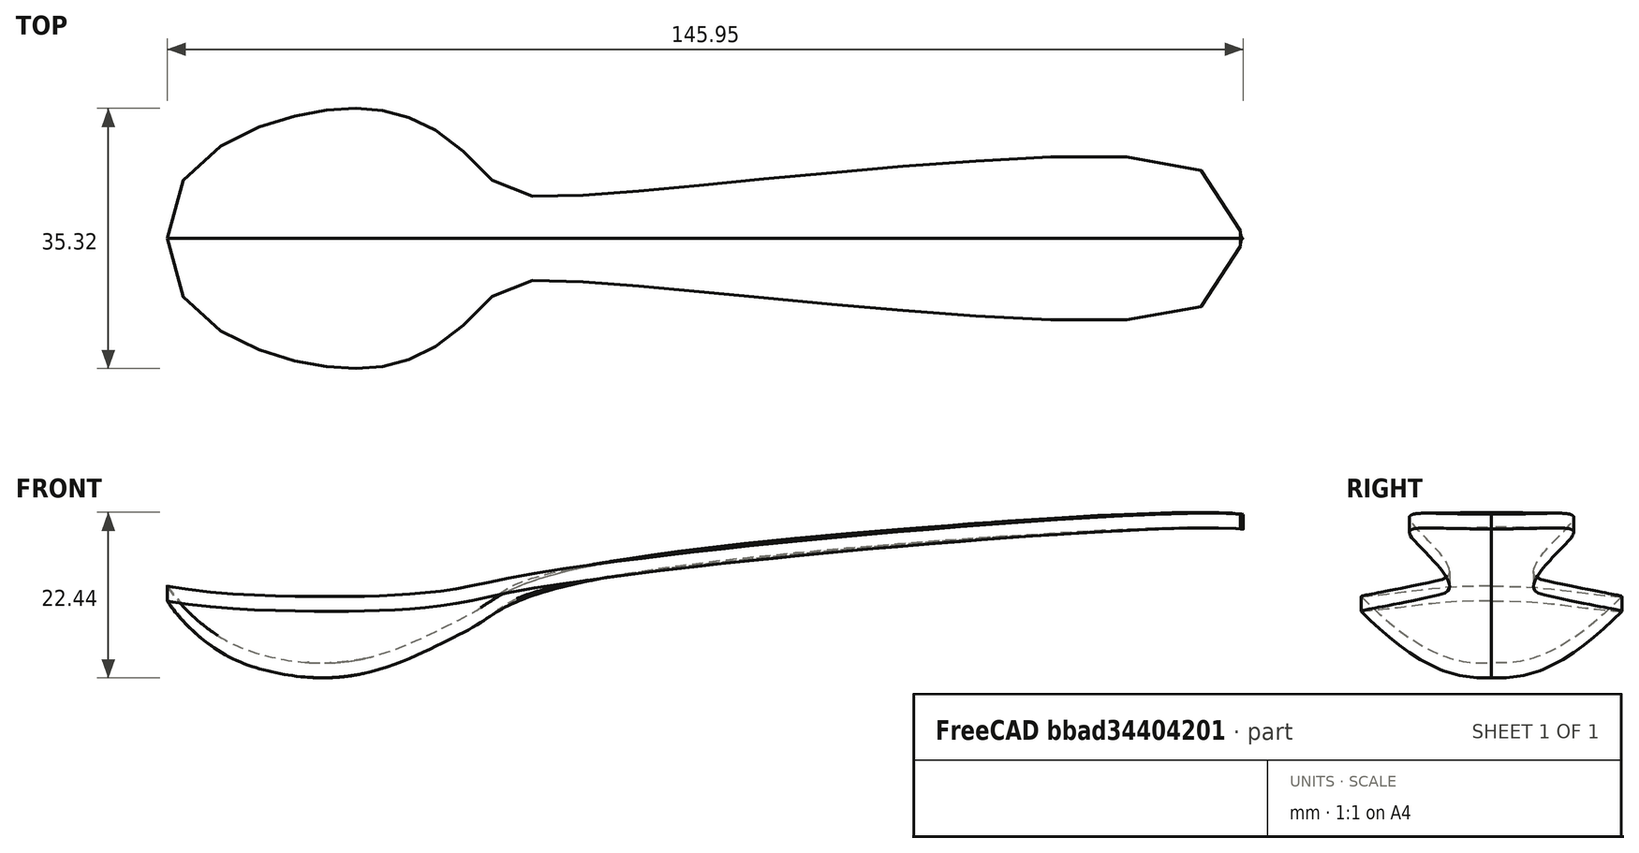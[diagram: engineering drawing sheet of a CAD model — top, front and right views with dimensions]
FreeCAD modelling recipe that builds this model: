
FCSTD DOCUMENT  (FreeCAD 0.20R29603 (Git))
Label: spoonFinalUsingCurves
License: All rights reserved
LicenseURL: http://en.wikipedia.org/wiki/All_rights_reserved
objects: Part::FeaturePython×9, Sketcher::SketchObject×7, App::LinkGroup×2, PartDesign::Body×1, Part::Extrusion×1, Part::Mirroring×1, Part::MultiFuse×1
note: 20 computed .brp shape members not serialized (recipe doc carries the construction recipe); baked Part::Feature solids carry a one-line shape summary decoded from their .brp

FEATURE [Sketcher::SketchObject] Sketch  label="top"
  FullyConstrained = false
  MapMode = 5
  Support = -> [XY_Plane]
  sketch-geometry (29):
    g0-g10: Circle x11 (B-spline internal-alignment scaffolding for g11; pole/knot coordinates omitted)
    g11: BSplineCurve PolesCount=11 KnotsCount=9 Degree=3 IsPeriodic=0
    g12: GeomPoint X=-47.6871 Y=0 Z=0
    g13-g20: GeomPoint x8 (B-spline internal-alignment scaffolding for g11; pole/knot coordinates omitted)
    g21: LineSegment StartX=-47.6871 StartY=0 StartZ=0 EndX=97.8729 EndY=0 EndZ=0
    g22: GeomPoint X=-43.3739 Y=0 Z=0
    g23: GeomPoint X=-33.1869 Y=0 Z=0
    g24: GeomPoint X=-21.4164 Y=0 Z=0
    g25: GeomPoint X=-10.9538 Y=0 Z=0
    g26: GeomPoint X=-2.80499 Y=0 Z=0
    g27: GeomPoint X=89.548 Y=0 Z=0
    g28: GeomPoint X=1.42031 Y=0 Z=0
  constraints (18):
    c: Equal(g0, g1-g10) x10
    c: InternalAlignment(g0-g10 -> g11) x11
    c: InternalAlignment(g13-g20 -> g11) x8
    c: Vertical(g11,g1)
    c: Coincident(g11,g12)
    c: Vertical(g9,g11)
    c: DistanceX(g11,g11) = 145.56
    c: PointOnObject(g11,g-1)
    c: Coincident(g21,g11)
    c: Coincident(g21,g11)
    c: Horizontal(g21)
    c: PointOnObject(g22,g21)
    c: PointOnObject(g23,g21)
    c: PointOnObject(g24,g21)
    c: PointOnObject(g25,g21)
    c: PointOnObject(g26,g21)
    c: PointOnObject(g27,g21)
    c: PointOnObject(g28,g21)
FEATURE [PartDesign::Body] Body
  Group = -> [Sketch]
  Origin = -> Origin
FEATURE [Sketcher::SketchObject] Sketch004  label="frontMiddle"
  ExternalGeometry = -> [Sketch]
  FullyConstrained = false
  Placement = pos=(0,0,-1) rot=(1,0,0;1.5708rad)
  sketch-geometry (21):
    g0: GeomPoint X=229.589 Y=93.1021 Z=0
    g1: GeomPoint X=229.589 Y=93.1021 Z=0
    g2: GeomPoint X=229.589 Y=93.1021 Z=0
    g3: GeomPoint X=301.189 Y=90.2757 Z=0
    g4-g12: Circle x9 (B-spline internal-alignment scaffolding for g13; pole/knot coordinates omitted)
    g13: BSplineCurve PolesCount=9 KnotsCount=7 Degree=3 IsPeriodic=0
    g14-g20: GeomPoint x7 (B-spline internal-alignment scaffolding for g13; pole/knot coordinates omitted)
  constraints (5):
    c: Weight(g4) = 1
    c: Coincident(g13,g-3)
    c: Equal(g4, g5-g12) x8
    c: InternalAlignment(g4-g12 -> g13) x9
    c: InternalAlignment(g14-g20 -> g13) x7
FEATURE [Sketcher::SketchObject] Sketch005  label="ffrontSide"
  AttachmentOffset = pos=(0,0,-20) rot=(0,0,1;0rad)
  ExternalGeometry = -> [Sketch,Sketch004]
  FullyConstrained = false
  MapMode = 3
  Placement = pos=(0,20,-4.4e-15) rot=(1,0,0;1.5708rad)
  Support = -> [Sketch]
  sketch-geometry (18):
    g0-g8: Circle x9 (B-spline internal-alignment scaffolding for g9; pole/knot coordinates omitted)
    g9: BSplineCurve PolesCount=9 KnotsCount=7 Degree=3 IsPeriodic=0
    g10-g16: GeomPoint x7 (B-spline internal-alignment scaffolding for g9; pole/knot coordinates omitted)
    g17: LineSegment StartX=98.2633 StartY=9.6068 StartZ=0 EndX=98.2633 EndY=0 EndZ=0
  constraints (7):
    c: Weight(g0) = 1
    c: Equal(g0, g1-g8) x8
    c: InternalAlignment(g0-g8 -> g9) x9
    c: InternalAlignment(g10-g16 -> g9) x7
    c: Coincident(g17,g9)
    c: Vertical(g17)
    c: Coincident(g-4,g9)
FEATURE [Part::FeaturePython] Mixed_curve  label="MixedMiddle"  # WARN: FeaturePython — macro-defined, semantics opaque (R4)
  Active = false
  ApproxTolerance = 0.001
  Continuity = 5
  DegreeMax = 5
  DegreeMin = 3
  Direction1 = (0,0,0)
  Direction2 = (0,0,0)
  FillFace1 = false
  FillFace2 = false
  Parametrization = 0
  Samples = 100
  Shape1 = -> Sketch004
  Shape2 = -> Sketch
FEATURE [Part::FeaturePython] Mixed_curve001  label="MixedSide"  # WARN: FeaturePython — macro-defined, semantics opaque (R4)
  Active = false
  ApproxTolerance = 0.001
  Continuity = 5
  DegreeMax = 5
  DegreeMin = 3
  Direction1 = (0,0,0)
  Direction2 = (0,0,0)
  FillFace1 = false
  FillFace2 = false
  Parametrization = 0
  Samples = 100
  Shape1 = -> Sketch005
  Shape2 = -> Sketch
FEATURE [Part::FeaturePython] Line  # WARN: FeaturePython — macro-defined, semantics opaque (R4)
  Vertex1 = -> Mixed_curve001 [Vertex1]
  Vertex2 = -> Sketch004 [Vertex1]
FEATURE [Part::FeaturePython] Line001  # WARN: FeaturePython — macro-defined, semantics opaque (R4)
  Vertex1 = -> Mixed_curve001 [Vertex2]
  Vertex2 = -> Sketch004 [Vertex2]
FEATURE [Part::FeaturePython] Profile  label="Profile1"  # WARN: FeaturePython — macro-defined, semantics opaque (R4)
  Edge1 = -> Mixed_curve001 [Edge1]
  Edge2 = -> Sketch004 [Edge1]
  MainAxis = (0,0,0)
  Parameter1 = 0.07
  Parameter2 = 0.069036
FEATURE [Part::FeaturePython] Profile001  label="Profile2 "  # WARN: FeaturePython — macro-defined, semantics opaque (R4)
  Edge1 = -> Mixed_curve001 [Edge1]
  Edge2 = -> Sketch004 [Edge1]
  MainAxis = (0,0,0)
  Parameter1 = 0.17
  Parameter2 = 0.269316
FEATURE [Part::FeaturePython] Profile002  label="Profile3"  # WARN: FeaturePython — macro-defined, semantics opaque (R4)
  Edge1 = -> Mixed_curve001 [Edge1]
  Edge2 = -> Sketch004 [Edge1]
  MainAxis = (0,0,0)
  Parameter1 = 0.291991
  Parameter2 = 0.599792
FEATURE [Part::FeaturePython] Profile003  label="Profile4"  # WARN: FeaturePython — macro-defined, semantics opaque (R4)
  Edge1 = -> Mixed_curve001 [Edge1]
  Edge2 = -> Sketch004 [Edge1]
  MainAxis = (0,0,-1)
  Parameter1 = 0.8965
  Parameter2 = 0.965683
FEATURE [Sketcher::SketchObject] Sketch012  label="Sketch1"
  ExternalGeometry = -> [Profile]
  FullyConstrained = false
  MapMode = 5
  Placement = pos=(-41.9192,-2.03518,0) rot=(0.55868,0.586462,0.586462;2.12263rad)
  Support = -> [Profile]
  sketch-geometry (11):
    g0: GeomPoint X=-117.774 Y=-70.6272 Z=0
    g1: GeomPoint X=-117.774 Y=-70.6272 Z=0
    g2: GeomPoint X=-117.774 Y=-70.6272 Z=0
    g3: GeomPoint X=-69.665 Y=-60.183 Z=0
    g4-g7: Circle x4 (B-spline internal-alignment scaffolding for g8; pole/knot coordinates omitted)
    g8: BSplineCurve PolesCount=4 KnotsCount=2 Degree=3 IsPeriodic=0
    g9: GeomPoint X=13.0771 Y=-0.861292 Z=0
    g10: GeomPoint X=2.03758 Y=-6.01694 Z=0
  constraints (10):
    c: Weight(g4) = 1
    c: Coincident(g8,g-3)
    c: Equal(g4,g5)
    c: Equal(g4,g6)
    c: Equal(g4,g7)
    c: Coincident(g8,g-3)
    c: InternalAlignment(g4-g7 -> g8) x4
    c: InternalAlignment(g9,g8)
    c: InternalAlignment(g10,g8)
    c: Horizontal(g6,g8)
FEATURE [Sketcher::SketchObject] Sketch013  label="Sketch2"
  ExternalGeometry = -> [Profile001]
  FullyConstrained = false
  MapMode = 5
  Placement = pos=(-26.1161,0.530872,0) rot=(0.585173,0.573399,0.573399;2.0827rad)
  Support = -> [Profile001]
  sketch-geometry (7):
    g0-g3: Circle x4 (B-spline internal-alignment scaffolding for g4; pole/knot coordinates omitted)
    g4: BSplineCurve PolesCount=4 KnotsCount=2 Degree=3 IsPeriodic=0
    g5: GeomPoint X=16.9177 Y=-1.53827 Z=0
    g6: GeomPoint X=-0.530981 Y=-10.5595 Z=0
  constraints (10):
    c: Weight(g0) = 1
    c: Coincident(g4,g-3)
    c: Equal(g0,g1)
    c: Equal(g0,g2)
    c: Equal(g0,g3)
    c: Coincident(g4,g-3)
    c: InternalAlignment(g0-g3 -> g4) x4
    c: InternalAlignment(g5,g4)
    c: InternalAlignment(g6,g4)
    c: Horizontal(g2,g4)
FEATURE [Sketcher::SketchObject] Sketch014  label="Sketch3"
  ExternalGeometry = -> [Profile002]
  FullyConstrained = false
  MapMode = 5
  Placement = pos=(-5.92794,-0.275172,0) rot=(0.559498,0.586072,0.586072;2.12138rad)
  Support = -> [Profile002]
  sketch-geometry (7):
    g0-g3: Circle x4 (B-spline internal-alignment scaffolding for g4; pole/knot coordinates omitted)
    g4: BSplineCurve PolesCount=4 KnotsCount=2 Degree=3 IsPeriodic=0
    g5: GeomPoint X=10.9999 Y=-0.103713 Z=0
    g6: GeomPoint X=0.275468 Y=-3.52099 Z=0
  constraints (10):
    c: Weight(g0) = 1
    c: Coincident(g4,g-3)
    c: Equal(g0,g1)
    c: Equal(g0,g2)
    c: Equal(g0,g3)
    c: Coincident(g4,g-3)
    c: InternalAlignment(g0-g3 -> g4) x4
    c: InternalAlignment(g5,g4)
    c: InternalAlignment(g6,g4)
    c: Horizontal(g2,g4)
FEATURE [Sketcher::SketchObject] Sketch015  label="Sketch4"
  ExternalGeometry = -> [Profile003]
  FullyConstrained = true
  MapMode = 5
  Placement = pos=(87.7775,9.38443,0) rot=(0.618317,-0.555736,-0.555736;2.03403rad)
  Support = -> [Profile003]
  sketch-geometry (1):
    g0: LineSegment StartX=-1.16262 StartY=9.64739 StartZ=0 EndX=9.43791 EndY=9.83754 EndZ=0
  constraints (2):
    c: Coincident(g0,g-3)
    c: Coincident(g0,g-3)
FEATURE [Part::FeaturePython] Gordon  # WARN: FeaturePython — macro-defined, semantics opaque (R4)
  FlipNormal = false
  MaxCtrlPts = 80
  Output = 0
  SamplesU = 16
  SamplesV = 16
  Sources = -> [Line,Line001,Sketch012,Sketch013,Sketch014,Sketch015,Mixed_curve001,Sketch004]
  Tol2D = 1e-05
  Tol3D = 0.01
FEATURE [Part::Extrusion] Extrude  label="half spoon"
  Base = -> Gordon
  Dir = (0,0,1)
  DirMode = 0
  FaceMakerClass = Part::FaceMakerBullseye
  LengthFwd = 2
  LengthRev = 0
  Solid = false
  Symmetric = false
FEATURE [Part::Mirroring] Part__Mirroring  label="Extrude (Mirror #1)"
  Base = (25.2881,5.96046e-08,0.66165)
  Normal = (0,1,-1.19209e-07)
  Source = -> Extrude
FEATURE [App::LinkGroup] LinkGroup  label="Profiles "
  ElementList = -> [Profile,Profile001,Profile002,Profile003]
  LinkMode = 0
FEATURE [App::LinkGroup] LinkGroup001  label="ribs"
  ElementList = -> [Line,Line001,Sketch012,Sketch013,Sketch014,Sketch015]
  LinkMode = 0
FEATURE [Part::MultiFuse] Fusion  label="spoon"
  Refine = true
  Shapes = -> [Part__Mirroring,Extrude]
